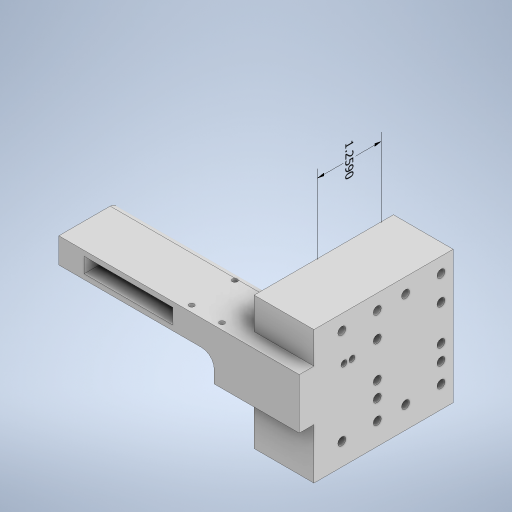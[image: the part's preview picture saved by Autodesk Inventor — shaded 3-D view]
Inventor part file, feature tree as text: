
AUTODESK INVENTOR PART (.ipt)
format: ipt  version: 2024.2 (Build 282272000, 272)  size: 518,144 bytes
history: native  units: in
note: dims shown in document units (in); Inventor stores cm internally (conversion verified against a paired STEP export)
features: extrude x20, sketch x20, projected_geometry x6, fillet x3, other x2
ambient origin geometry x8: Origin, YZ Plane, XZ Plane, XY Plane, X Axis, Y Axis, Z Axis, Center Point
bodies: Solid1 (feature_tree)
feature tree (51):
  other  "Annotations"
  extrude  "Extrusion1"  Depth=2.0in
  extrude  "Extrusion2"  Depth=1.5in
  extrude  "Extrusion3"  Depth=1.5in TaperAngle=0.0deg
  extrude  "Extrusion4"  Depth=0.5in
  fillet  "Fillet1"  Radius=0.25in
  extrude  "Extrusion5"  Depth=1.5in
  extrude  "Extrusion7"  Depth=0.118in
  extrude  "Extrusion8"  TaperAngle=0.0deg  [1 undecoded]
  extrude  "Extrusion9"  Depth=0.539in TaperAngle=0.0deg
  extrude  "Extrusion10"  Depth=0.787in
  extrude  "Extrusion11"  Depth=0.5in TaperAngle=0.0deg
  extrude  "Extrusion12"  Depth=0.157in
  extrude  "Extrusion13"  Depth=0.157in
  extrude  "Extrusion14"  Depth=1.259in
  extrude  "Extrusion15"  Depth=0.25in
  extrude  "Extrusion16"  TaperAngle=0.0deg  [1 undecoded]
  extrude  "Extrusion17"  Depth=0.1in
  extrude  "Extrusion18"  Depth=0.1in
  extrude  "Extrusion19"  Depth=0.6in
  extrude  "Extrusion20"  Depth=0.85in
  extrude  "Extrusion21"  Depth=0.15in
  fillet  "Fillet4"  [1 undecoded]
  fillet  "Fillet5"  [1 undecoded]
  sketch  "Sketch1"  dims[d0=2.75in d1=2.0in]
  sketch  "Sketch2"  dims[d2=1.5in d3=0.0in d4=1.375in]
  sketch  "Sketch3"  dims[d5=1.57in d6=1.5in d7=0.0in]
  sketch  "Sketch4"  dims[d9=0.5in d10=0.5in d11=0.25in]
  sketch  "Sketch5"  dims[d12=1.5in d13=0.0in d14=0.157in]
  projected_geometry  "Projected Loop1"
  sketch  "Sketch9"  dims[d15=0.118in d16=0.118in]
  projected_geometry  "Projected Loop2"
  sketch  "Sketch10"  dims[d17=0.125in d18=0.0in d19=0.0in]
  sketch  "Sketch11"  dims[d20=0.125in d21=0.539in d22=0.0in]
  sketch  "Sketch12"  dims[d23=0.2in d24=0.787in]
  sketch  "Sketch13"  dims[d25=1.069in d41=0.5in d42=0.0in]
  sketch  "Sketch14"  dims[d43=0.157in d44=0.157in]
  sketch  "Sketch15"  dims[d45=0.157in d46=0.157in]
  sketch  "Sketch16"  dims[d47=1.259in d48=1.259in]
  projected_geometry  "Projected Loop3"
  sketch  "Sketch17"  dims[d49=0.25in d50=0.25in]
  sketch  "Sketch18"  dims[d51=0.0in d52=0.0in d53=0.0in]
  projected_geometry  "Projected Loop4"
  sketch  "Sketch19"  dims[d54=0.1in d55=0.1in]
  projected_geometry  "Projected Loop5"
  sketch  "Sketch20"  dims[d56=0.1in d57=0.1in]
  projected_geometry  "Projected Loop6"
  sketch  "Sketch21"  dims[d58=0.0in d59=0.6in]
  sketch  "Sketch22"  dims[d60=0.6in d61=0.85in]
  sketch  "Sketch23"  dims[d62=0.0in d63=0.5in d64=0.0in d65=0.0in d66=0.0in d67=1.75in d68=0.625in d69=0.0in d70=0.157in d71=0.157in d72=0.49in d73=0.49in d74=0.0in d75=0.157in d76=0.157in d77=1.0in d78=0.0in d79=0.5in d80=0.0in d81=0.157in d82=0.0in d83=1.889in d84=1.889in d85=0.0in d86=0.0in d87=2.0in d88=0.0in d89=0.1in d90=0.1in d91=0.1in d92=0.1in d93=0.6in d94=0.6in d95=0.85in d96=2.25in d97=0.125in d98=0.125in d99=0.0in d100=0.0in d101=0.0in d102=0.5in d103=0.0in d104=1.0in d105=0.0in d106=1.0in d107=0.0in d109=0.241in d110=0.157in d111=0.157in d112=1.259in d113=0.7in d114=1.0in d115=0.0in d116=0.157in d117=1.259in d118=0.0in d119=0.0in d120=1.889in d121=0.0in d122=0.0in d123=0.1in d124=0.1in d125=0.5in d126=0.0in d127=0.0in d128=1.75in d129=0.15in d130=0.15in d108=1.259in]
  other  "Linear Dimension 1"
note: 4 required parameter values undecoded (feature->parameter linkage not recoverable at this tier; creation-order binding heuristic only, values carry confidence <= 0.55)
